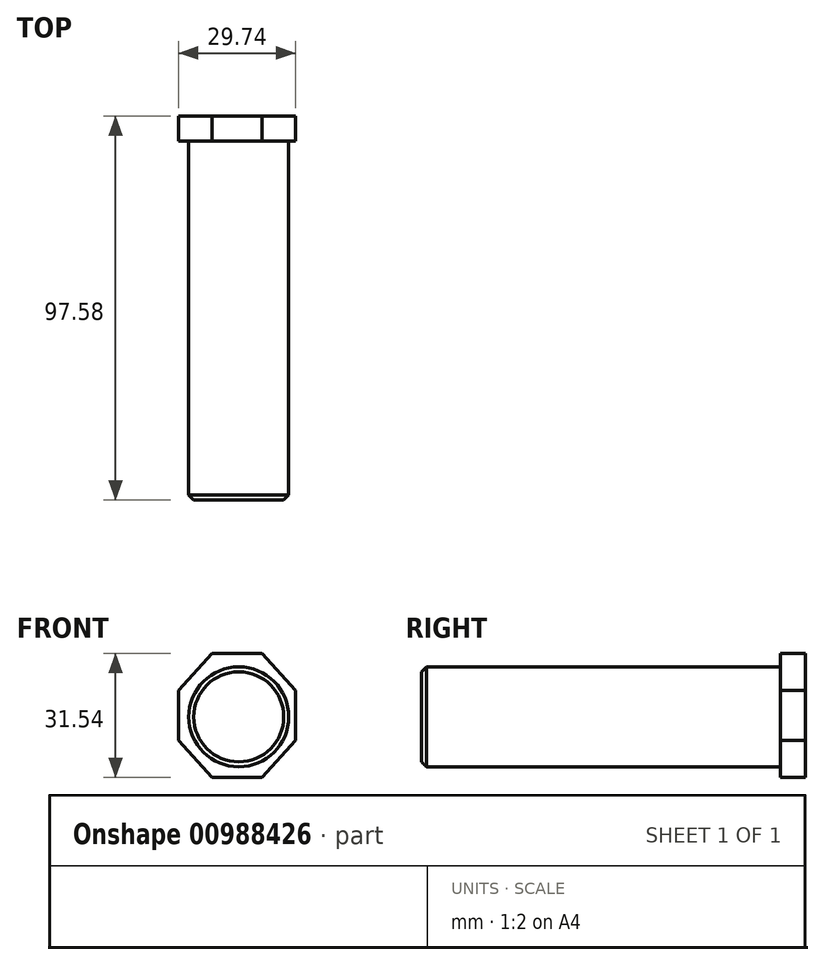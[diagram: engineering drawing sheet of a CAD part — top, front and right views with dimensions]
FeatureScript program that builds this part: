
annotation { "Feature Type Name" : "Feature", "Feature Type Description" : "" }
export const myFeature = defineFeature(function(context is Context, id is Id, definition is map)
    precondition{}
    {
        {
            assignVariable(context, id + "F0", {"name" : "FlangeWidth", "anyValue" : 29.74 * mm});
        }
        {
            assignVariable(context, id + "F1", {"name" : "FittingEyeBoltThickness", "anyValue" : 25.4 * mm});
        }
        {
            var Q0;
            Q0=qCreatedBy(makeId("Front.planeOp"),FACE);
            var sketch = newSketch(context, id + "F2", { "sketchPlane" : qUnion([Q0])});
            skCircle(sketch, "E0", {"center": v(0, 0) * mm, "radius": 12.7 * mm});
            skSolve(sketch);
        }
        {
            var Q0;
            Q0=makeQuery(id+"F2.imprint","IMPRINT",FACE,{"disambiguationData":[TD([[makeQuery(id+"F2.imprint","IMPRINT",EDGE,{"derivedFrom":sQuery(id+"F2.wireOp",EDGE,"E0")}),1.0]])]});
            extrude(context, id + "F3", {"entities" : qUnion([Q0]), "depth" : getVariable(context, 'FittingEyeBoltThickness') + getVariable(context, 'FlangeWidth') * 2 + 6.35 * mm, "offsetDistance" : 25.4 * mm});
        }
        {
            var Q0;
            Q0=qCreatedBy(makeId("Front.planeOp"),FACE);
            var sketch = newSketch(context, id + "F4", { "sketchPlane" : qUnion([Q0])});
            skLineSegment(sketch, "E1", {"start": v(-6.78, -15.43) * mm, "end": v(5.92, -15.43) * mm});
            skLineSegment(sketch, "E2", {"start": v(5.92, -15.43) * mm, "end": v(14.44, -6) * mm});
            skLineSegment(sketch, "E3", {"start": v(14.44, -6) * mm, "end": v(14.44, 6.7) * mm});
            skLineSegment(sketch, "E4", {"start": v(14.44, 6.7) * mm, "end": v(5.92, 16.1) * mm});
            skLineSegment(sketch, "E5", {"start": v(5.92, 16.1) * mm, "end": v(-6.78, 16.1) * mm});
            skLineSegment(sketch, "E6", {"start": v(-6.78, 16.1) * mm, "end": v(-15.3, 6.7) * mm});
            skLineSegment(sketch, "E7", {"start": v(-15.3, 6.7) * mm, "end": v(-15.3, -6) * mm});
            skLineSegment(sketch, "E8", {"start": v(-15.3, -6) * mm, "end": v(-6.78, -15.43) * mm});
            skSolve(sketch);
        }
        {
            var Q0;
            Q0 = qSketchRegion(id + "F4", true);
            extrude(context, id + "F5", {"entities" : qUnion([Q0]), "operationType" : NewBodyOperationType.ADD, "oppositeDirection" : true, "depth" : 6.35 * mm, "offsetDistance" : 25.4 * mm});
        }
        {
            var Q0;
            Q0=makeQuery(id+"F3.opExtrude","CAP_EDGE",EDGE,{"disambiguationData":[OSD([sQuery(id+"F2.wireOp",EDGE,"E0")])],"isStart":false});
            chamfer(context, id + "F6", {"entities" : qUnion([Q0]), "width" : 1.27 * mm, "tangentPropagation" : true});
        }
    });
